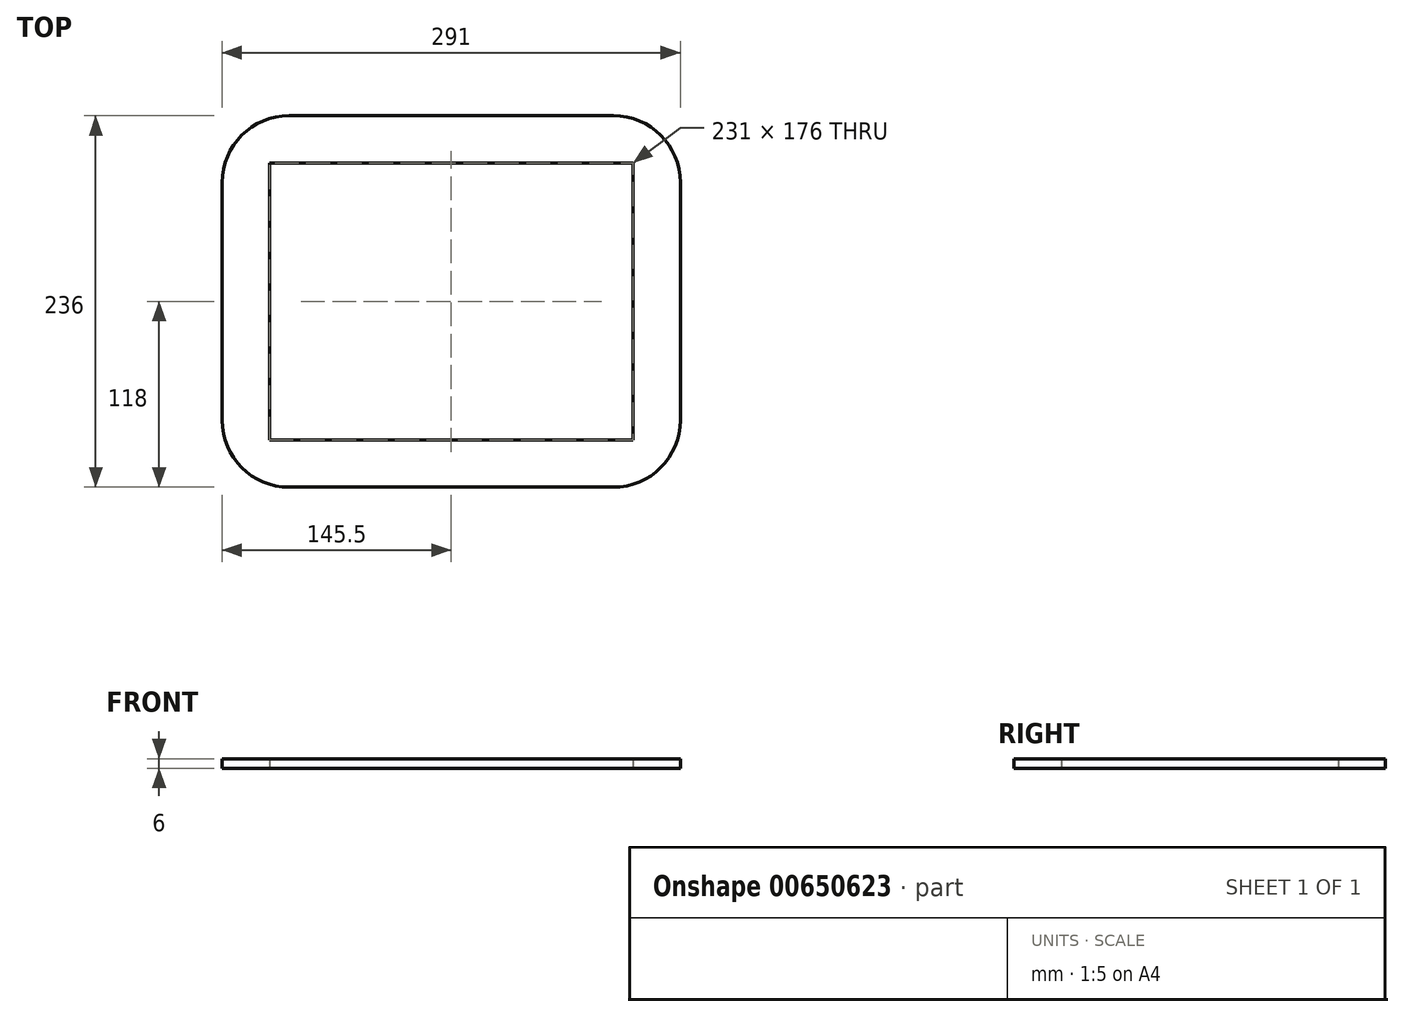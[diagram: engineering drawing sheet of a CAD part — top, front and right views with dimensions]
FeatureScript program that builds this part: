
annotation { "Feature Type Name" : "Feature", "Feature Type Description" : "" }
export const myFeature = defineFeature(function(context is Context, id is Id, definition is map)
    precondition{}
    {
        {
            var Q0;
            Q0=qCreatedBy(makeId("Top.planeOp"),FACE);
            var sketch = newSketch(context, id + "F0", { "sketchPlane" : qUnion([Q0])});
            skLineSegment(sketch, "E0.bottom", {"start": v(-103, 118) * mm, "end": v(103, 118) * mm});
            skLineSegment(sketch, "E0.top", {"start": v(-103, -118) * mm, "end": v(103, -118) * mm});
            skLineSegment(sketch, "E0.left", {"start": v(-145.5, 75.5) * mm, "end": v(-145.5, -75.5) * mm});
            skLineSegment(sketch, "E0.right", {"start": v(145.5, 75.5) * mm, "end": v(145.5, -75.5) * mm});
            skPoint(sketch, "E0.middle", {"position": v(0, 0) * mm});
            skLineSegment(sketch, "E1.bottom", {"start": v(-115.5, 88) * mm, "end": v(115.5, 88) * mm});
            skLineSegment(sketch, "E1.top", {"start": v(-115.5, -88) * mm, "end": v(115.5, -88) * mm});
            skLineSegment(sketch, "E1.left", {"start": v(-115.5, 88) * mm, "end": v(-115.5, -88) * mm});
            skLineSegment(sketch, "E1.right", {"start": v(115.5, 88) * mm, "end": v(115.5, -88) * mm});
            skLineSegment(sketch, "E2.bottom", {"start": v(-114.5, 87) * mm, "end": v(114.5, 87) * mm});
            skLineSegment(sketch, "E2.top", {"start": v(-114.5, -87) * mm, "end": v(114.5, -87) * mm});
            skLineSegment(sketch, "E2.left", {"start": v(-114.5, 87) * mm, "end": v(-114.5, -87) * mm});
            skLineSegment(sketch, "E2.right", {"start": v(114.5, 87) * mm, "end": v(114.5, -87) * mm});
            skPoint(sketch, "E3.visualSharp", {"position": v(-145.5, 118) * mm});
            skArc(sketch, "E3.filletArc", {"start": v(-103, 118) * mm, "mid": v(-133.05, 105.55) * mm, "end": v(-145.5, 75.5) * mm});
            skPoint(sketch, "E4.visualSharp", {"position": v(145.5, 118) * mm});
            skArc(sketch, "E4.filletArc", {"start": v(145.5, 75.5) * mm, "mid": v(133.05, 105.55) * mm, "end": v(103, 118) * mm});
            skPoint(sketch, "E5.visualSharp", {"position": v(145.5, -118) * mm});
            skArc(sketch, "E5.filletArc", {"start": v(103, -118) * mm, "mid": v(133.05, -105.55) * mm, "end": v(145.5, -75.5) * mm});
            skPoint(sketch, "E6.visualSharp", {"position": v(-145.5, -118) * mm});
            skArc(sketch, "E6.filletArc", {"start": v(-145.5, -75.5) * mm, "mid": v(-133.05, -105.55) * mm, "end": v(-103, -118) * mm});
            skSolve(sketch);
        }
        {
            var Q0;
            Q0=makeQuery(id+"F0.imprint","IMPRINT",FACE,{"disambiguationData":[TD([[makeQuery(id+"F0.imprint","IMPRINT",EDGE,{"derivedFrom":sQuery(id+"F0.wireOp",EDGE,"E0.bottom")}),-1.0]])]});
            extrude(context, id + "F1", {"entities" : qUnion([Q0]), "depth" : 6 * mm, "offsetDistance" : 25 * mm});
        }
    });
